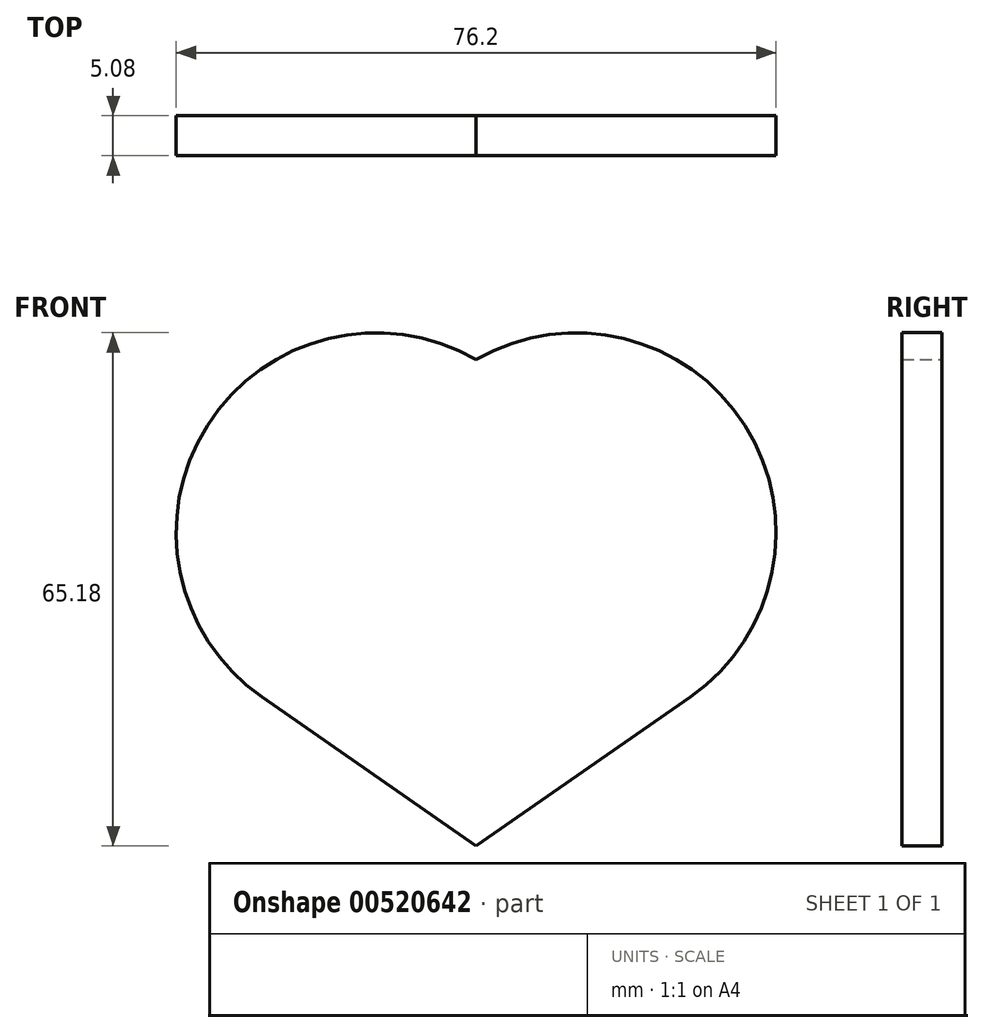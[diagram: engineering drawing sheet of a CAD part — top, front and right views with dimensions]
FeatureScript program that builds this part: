
annotation { "Feature Type Name" : "Feature", "Feature Type Description" : "" }
export const myFeature = defineFeature(function(context is Context, id is Id, definition is map)
    precondition{}
    {
        {
            var Q0;
            Q0=qCreatedBy(makeId("Front.planeOp"),FACE);
            var sketch = newSketch(context, id + "F0", { "sketchPlane" : qUnion([Q0])});
            skCircle(sketch, "E0", {"center": v(0, 0) * mm, "radius": 25.4 * mm});
            skCircle(sketch, "E1", {"center": v(25.4, 0) * mm, "radius": 25.4 * mm});
            skPoint(sketch, "E2", {"position": v(12.7, -22) * mm});
            skLineSegment(sketch, "E3", {"start": v(12.7, -22) * mm, "end": v(12.7, -39.78) * mm});
            skLineSegment(sketch, "E4", {"start": v(12.7, -39.78) * mm, "end": v(-14.5, -20.85) * mm});
            skLineSegment(sketch, "E5", {"start": v(12.7, -39.78) * mm, "end": v(39.9, -20.85) * mm});
            skSolve(sketch);
        }
        {
            var Q0;
            {var subQ5=sQuery(id+"F0.wireOp",EDGE,"VGXMVorV-Bhka-XHRI-ycMi-C0qwzemh4LBb");Q0=makeQuery(id+"F0.imprint","IMPRINT",FACE,{"disambiguationData":[TD([[makeQuery(id+"F0.imprint","IMPRINT",EDGE,{"derivedFrom":subQ5}),1.0]])]});}
            var Q1;
            {var subQ0=sQuery(id+"F0.wireOp",EDGE,"XMDcBOJK-KxLS-55VM-hwmy-Po1coEzqak9t");var subQ1=sQuery(id+"F0.wireOp",EDGE,"E0");var subQ2=makeQuery(id+"F0.imprint","INTERSECT",VERTEX,{"disambiguationData":[OD(0.0)],"derivedFrom":[subQ1,subQ0]});Q1=makeQuery(id+"F0.imprint","IMPRINT",FACE,{"disambiguationData":[TD([[makeQuery(id+"F0.imprint","IMPRINT",EDGE,{"disambiguationData":[TD([[subQ2,1.0]])],"derivedFrom":subQ1}),1.0]])]});}
            var Q2;
            {var subQ0=sQuery(id+"F0.wireOp",EDGE,"E1");var subQ1=sQuery(id+"F0.wireOp",EDGE,"E0");var subQ2=makeQuery(id+"F0.imprint","INTERSECT",VERTEX,{"disambiguationData":[OD(0.0)],"derivedFrom":[subQ1,subQ0]});Q2=makeQuery(id+"F0.imprint","IMPRINT",FACE,{"disambiguationData":[TD([[makeQuery(id+"F0.imprint","IMPRINT",EDGE,{"disambiguationData":[TD([[subQ2,1.0]])],"derivedFrom":subQ1}),-1.0]])]});}
            var Q3;
            {var subQ0=sQuery(id+"F0.wireOp",EDGE,"E1");var subQ1=sQuery(id+"F0.wireOp",EDGE,"E0");var subQ2=makeQuery(id+"F0.imprint","INTERSECT",VERTEX,{"disambiguationData":[OD(0.0)],"derivedFrom":[subQ1,subQ0]});Q3=makeQuery(id+"F0.imprint","IMPRINT",FACE,{"disambiguationData":[TD([[makeQuery(id+"F0.imprint","IMPRINT",EDGE,{"disambiguationData":[TD([[subQ2,1.0]])],"derivedFrom":subQ1}),1.0]])]});}
            extrude(context, id + "F1", {"entities" : qUnion([Q0, Q1, Q2, Q3]), "depth" : 2.54 * mm, "offsetDistance" : 25.4 * mm});
        }
        {
            var Q0;
            Q0=qSketchRegion(id+"F0",true);
            extrude(context, id + "F2", {"entities" : qUnion([Q0]), "operationType" : NewBodyOperationType.ADD, "depth" : 5.08 * mm, "offsetDistance" : 25.4 * mm});
        }
    });
